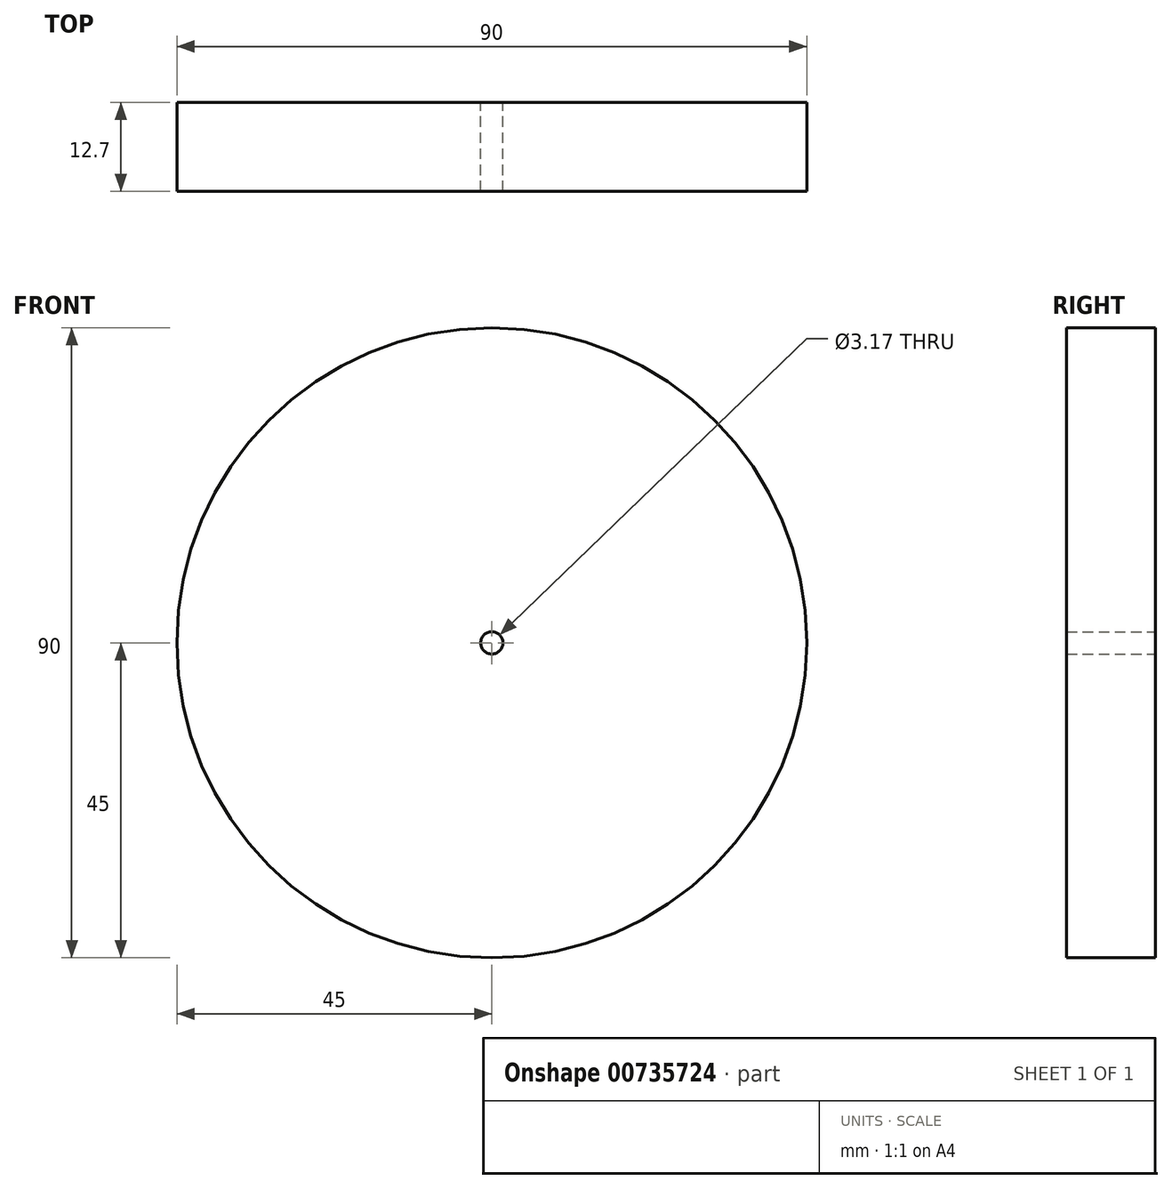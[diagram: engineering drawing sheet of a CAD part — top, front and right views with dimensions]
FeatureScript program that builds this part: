
annotation { "Feature Type Name" : "Feature", "Feature Type Description" : "" }
export const myFeature = defineFeature(function(context is Context, id is Id, definition is map)
    precondition{}
    {
        {
            var Q0;
            Q0=qCreatedBy(makeId("Front.planeOp"),FACE);
            var sketch = newSketch(context, id + "F0", { "sketchPlane" : qUnion([Q0])});
            skPoint(sketch, "E0", {"position": v(0, 0) * mm});
            skCircle(sketch, "E1", {"center": v(0, 0) * mm, "radius": 45 * mm});
            skCircle(sketch, "E2", {"center": v(0, 0) * mm, "radius": 1.59 * mm});
            skSolve(sketch);
        }
        {
            var Q0;
            Q0=makeQuery(id+"F0.imprint","IMPRINT",FACE,{"disambiguationData":[TD([[makeQuery(id+"F0.imprint","IMPRINT",EDGE,{"derivedFrom":sQuery(id+"F0.wireOp",EDGE,"E1")}),1.0]])]});
            extrude(context, id + "F1", {"entities" : qUnion([Q0]), "depth" : 12.7 * mm, "offsetDistance" : 25.4 * mm});
        }
    });
